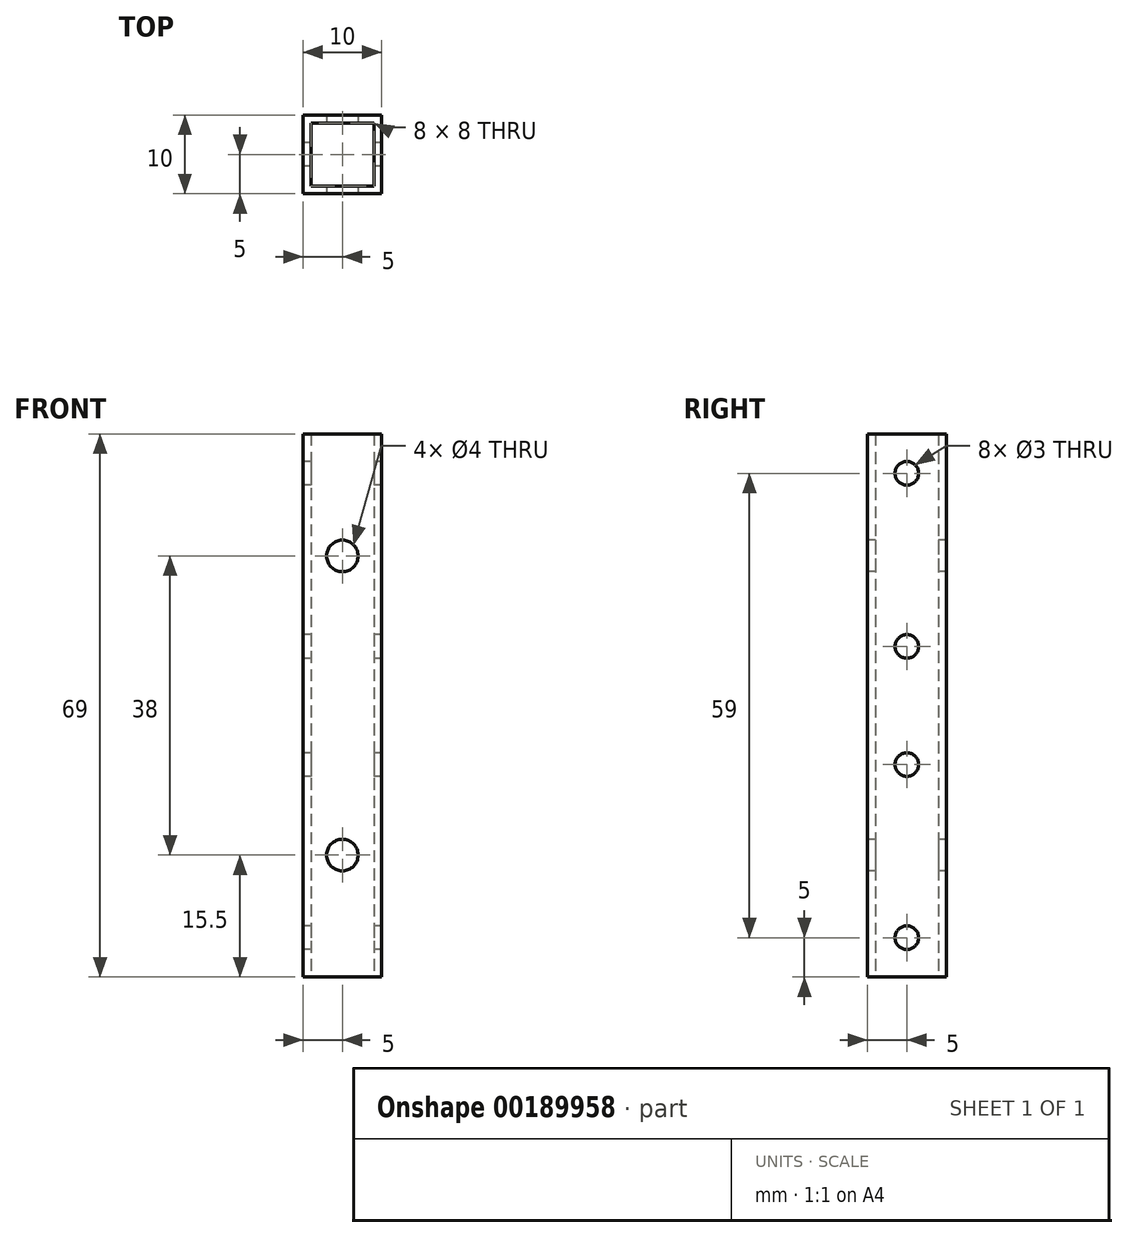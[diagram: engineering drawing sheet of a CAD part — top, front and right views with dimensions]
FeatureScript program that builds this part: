
annotation { "Feature Type Name" : "Feature", "Feature Type Description" : "" }
export const myFeature = defineFeature(function(context is Context, id is Id, definition is map)
    precondition{}
    {
        {
            var Q0;
            Q0=qCreatedBy(makeId("Top.planeOp"),FACE);
            var sketch = newSketch(context, id + "F0", { "sketchPlane" : qUnion([Q0])});
            skLineSegment(sketch, "E0.bottom", {"start": v(-5, -5) * mm, "end": v(5, -5) * mm});
            skLineSegment(sketch, "E0.top", {"start": v(-5, 5) * mm, "end": v(5, 5) * mm});
            skLineSegment(sketch, "E0.left", {"start": v(-5, -5) * mm, "end": v(-5, 5) * mm});
            skLineSegment(sketch, "E0.right", {"start": v(5, -5) * mm, "end": v(5, 5) * mm});
            skPoint(sketch, "E0.middle", {"position": v(0, 0) * mm});
            skLineSegment(sketch, "E1.bottom", {"start": v(-4, -4) * mm, "end": v(4, -4) * mm});
            skLineSegment(sketch, "E1.top", {"start": v(-4, 4) * mm, "end": v(4, 4) * mm});
            skLineSegment(sketch, "E1.left", {"start": v(-4, -4) * mm, "end": v(-4, 4) * mm});
            skLineSegment(sketch, "E1.right", {"start": v(4, -4) * mm, "end": v(4, 4) * mm});
            skSolve(sketch);
        }
        {
            var Q0;
            Q0 = qSketchRegion(id + "F0", true);
            extrude(context, id + "F1", {"entities" : qUnion([Q0]), "depth" : 69 * mm});
        }
        {
            var Q0;
            Q0=makeQuery(id+"F1.opExtrude","SWEPT_FACE",FACE,{"disambiguationData":[OSD([sQuery(id+"F0.wireOp",EDGE,"E0.bottom")])]});
            var sketch = newSketch(context, id + "F2", { "sketchPlane" : qUnion([Q0])});
            skLineSegment(sketch, "E2", {"start": v(0, 69) * mm, "end": v(0, 0) * mm, "construction": true});
            skLineSegment(sketch, "E3", {"start": v(-5, 34.5) * mm, "end": v(5, 34.5) * mm, "construction": true});
            skCircle(sketch, "E4", {"center": v(0, 15.5) * mm, "radius": 2 * mm});
            skCircle(sketch, "E5.MirrorC", {"center": v(0, 53.5) * mm, "radius": 2 * mm});
            skSolve(sketch);
        }
        {
            var Q0;
            Q0 = qSketchRegion(id + "F2", true);
            extrude(context, id + "F3", {"entities" : qUnion([Q0]), "operationType" : NewBodyOperationType.REMOVE, "oppositeDirection" : true, "depth" : 25 * mm});
        }
        {
            var Q0;
            Q0=makeQuery(id+"F1.opExtrude","SWEPT_FACE",FACE,{"disambiguationData":[OSD([sQuery(id+"F0.wireOp",EDGE,"E0.left")])]});
            var sketch = newSketch(context, id + "F4", { "sketchPlane" : qUnion([Q0])});
            skLineSegment(sketch, "E6", {"start": v(0, 69) * mm, "end": v(0, 0) * mm, "construction": true});
            skLineSegment(sketch, "E7", {"start": v(-5, 34.5) * mm, "end": v(5, 34.5) * mm, "construction": true});
            skCircle(sketch, "E8", {"center": v(0, 27) * mm, "radius": 1.5 * mm});
            skCircle(sketch, "E9.MirrorC", {"center": v(0, 42) * mm, "radius": 1.5 * mm});
            skCircle(sketch, "E10", {"center": v(0, 5) * mm, "radius": 1.5 * mm});
            skCircle(sketch, "E11.MirrorC", {"center": v(0, 64) * mm, "radius": 1.5 * mm});
            skSolve(sketch);
        }
        {
            var Q0;
            Q0 = qSketchRegion(id + "F4", true);
            extrude(context, id + "F5", {"entities" : qUnion([Q0]), "operationType" : NewBodyOperationType.REMOVE, "oppositeDirection" : true, "depth" : 25 * mm});
        }
    });
